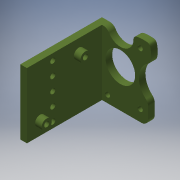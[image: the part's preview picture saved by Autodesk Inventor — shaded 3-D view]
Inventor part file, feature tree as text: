
AUTODESK INVENTOR PART (.ipt)
format: ipt  version: 2018 (Build 220112000, 112)  size: 268,800 bytes
history: native  units: in
note: dims shown in document units (in); Inventor stores cm internally (conversion verified against a paired STEP export)
features: extrude x11, sketch x9, other x3, fillet x1, projected_geometry x1, reference x1
ambient origin geometry x8: Origin, YZ Plane, XZ Plane, XY Plane, X Axis, Y Axis, Z Axis, Center Point
bodies: Solid1 (feature_tree)
feature tree (26):
  sketch  "Sketch1"  dims[d0=0.385in d1=0.385in]
  extrude  "Extrusion1"  Depth=0.385in
  extrude  "Extrusion2"  Depth=0.5in
  extrude  "Extrusion3"  Depth=0.5in
  extrude  "Extrusion4"  Depth=0.25in TaperAngle=0.0deg
  sketch  "Sketch4"  dims[d8=0.875in d9=0.25in d10=0.0in]
  extrude  "Extrusion5"  Depth=0.5in
  extrude  "Extrusion7"  Depth=2.0in
  extrude  "Extrusion8"  Depth=0.25in
  extrude  "Extrusion9"  Depth=1.036in
  fillet  "Fillet2"  Radius=1.122in
  extrude  "Extrusion10"  Depth=0.25in
  extrude  "Extrusion11"  Depth=2.0in
  extrude  "Extrusion12"  Depth=0.25in
  sketch  "Sketch2"  dims[d4=2.08in d5=0.5in]
  sketch  "Sketch3"  dims[d6=0.5in d7=0.5in]
  projected_geometry  "Projected Loop1"
  sketch  "Sketch5"  dims[d11=0.5in d12=0.0in d13=0.1935in]
  sketch  "Sketch6"  dims[d14=0.5in d15=0.0in d16=2.0in]
  sketch  "Sketch8"  dims[d17=0.25in d18=0.0in d19=0.768in]
  sketch  "Sketch9"  dims[d20=0.699in d21=1.036in d22=1.122in]
  sketch  "Sketch10"  dims[d23=2.5in d24=0.0in d25=0.25in d26=2.0in d27=0.25in d30=0.5in d31=0.95in d32=0.125in d33=0.1935in d38=1.0in d39=0.0in d40=0.75in d42=0.4in d43=1.0in d44=0.0in d46=1.25in d47=1.25in d48=1.25in d49=1.25in d50=2.0in d51=1.0in d54=1.0in d55=0.0in d56=0.25in d57=1.0in d58=1.25in d59=0.75in d60=0.25in d61=0.125in d62=0.5in d63=1.0in d64=0.0in d65=0.25in d66=0.25in d67=0.2in d68=1.9685in d70=0.5in d71=0.3937in d73=1.0in d75=1.0in d76=0.0in d77=0.1935in d78=0.25in d79=0.25in d80=1.9685in d82=0.5in d83=0.3937in d85=1.0in d87=1.0in d88=0.0in]
  reference  "Reference1"
  parser-record x1  (decoder bookkeeping rows leaked as tree rows — omitted from the tree; the rows remain in map.json)
  other  "Wheel Assembly Right.iam"
  other  "mounting plate:1"
note: 1 file-system path scrubbed to <path> (originals preserved in map.json)
